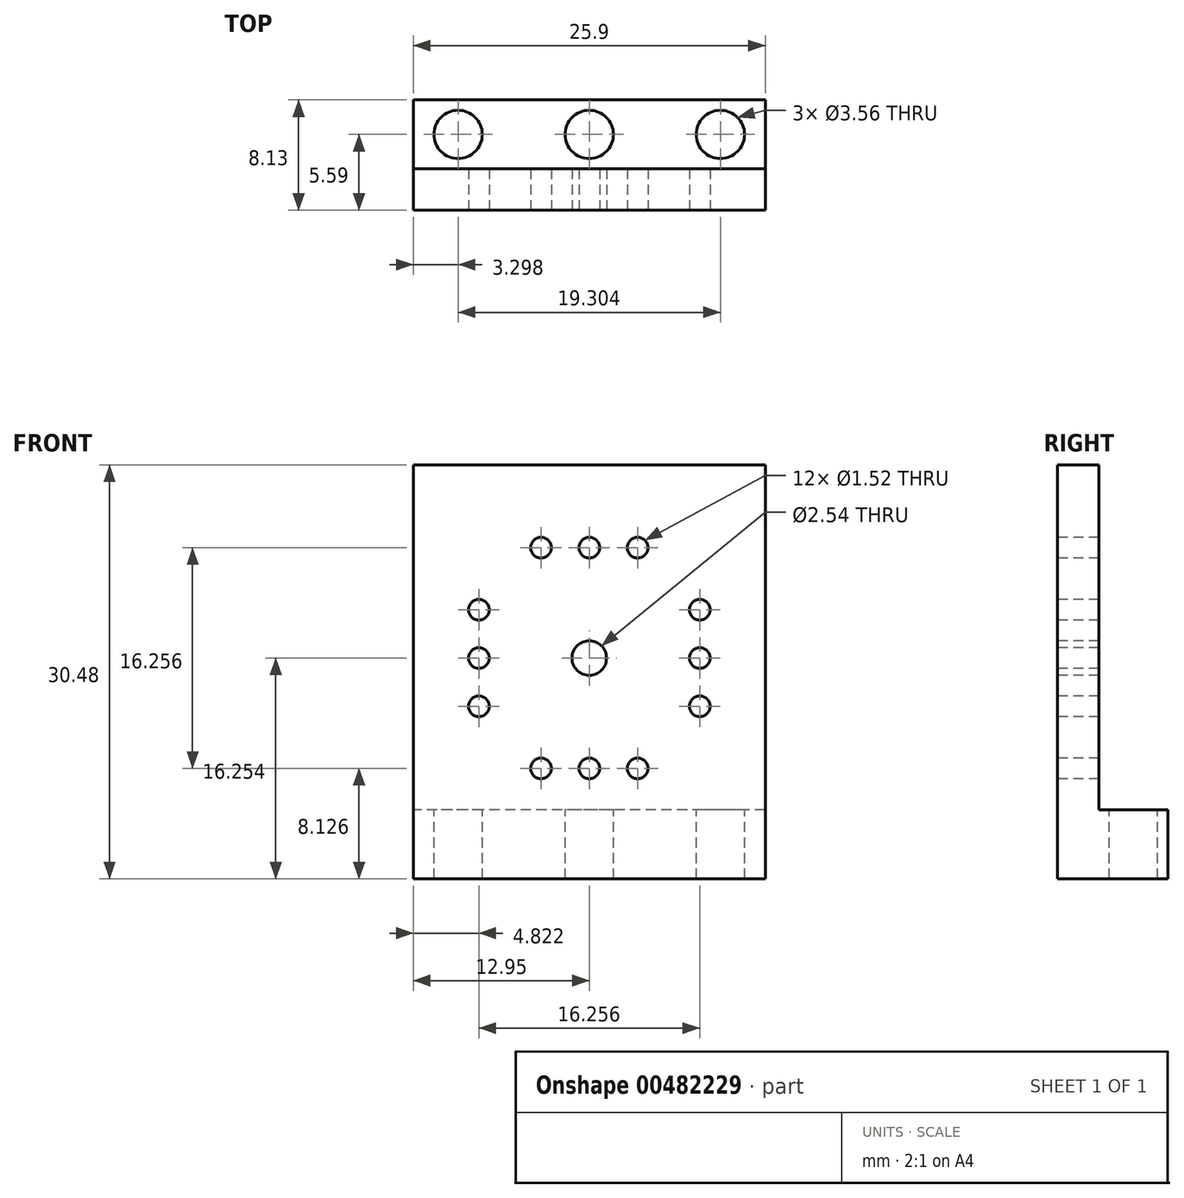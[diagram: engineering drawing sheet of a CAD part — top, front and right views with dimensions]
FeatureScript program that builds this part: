
annotation { "Feature Type Name" : "Feature", "Feature Type Description" : "" }
export const myFeature = defineFeature(function(context is Context, id is Id, definition is map)
    precondition{}
    {
        {
            var Q0;
            Q0=qCreatedBy(makeId("Top.planeOp"),FACE);
            var sketch = newSketch(context, id + "F0", { "sketchPlane" : qUnion([Q0])});
            skLineSegment(sketch, "E0.bottom", {"start": v(12.95, -2.54) * mm, "end": v(-12.95, -2.54) * mm});
            skLineSegment(sketch, "E0.top", {"start": v(12.95, 2.54) * mm, "end": v(-12.95, 2.54) * mm});
            skLineSegment(sketch, "E0.left", {"start": v(12.95, -2.54) * mm, "end": v(12.95, 2.54) * mm});
            skLineSegment(sketch, "E0.right", {"start": v(-12.95, -2.54) * mm, "end": v(-12.95, 2.54) * mm});
            skPoint(sketch, "E0.middle", {"position": v(0, 0) * mm});
            skSolve(sketch);
        }
        {
            var Q0;
            Q0=makeQuery(id+"F0.imprint","IMPRINT",FACE,{"disambiguationData":[TD([[makeQuery(id+"F0.imprint","IMPRINT",EDGE,{"derivedFrom":sQuery(id+"F0.wireOp",EDGE,"E0.bottom")}),-1.0]])]});
            extrude(context, id + "F1", {"entities" : qUnion([Q0]), "depth" : 3.05 * mm, "offsetDistance" : 25.4 * mm});
        }
        {
            var Q0;
            Q0=makeQuery(id+"F1.opExtrude","CAP_FACE",FACE,{"disambiguationData":[OSD([sQuery(id+"F0.wireOp",EDGE,"E0.bottom"),sQuery(id+"F0.wireOp",EDGE,"E0.top"),sQuery(id+"F0.wireOp",EDGE,"E0.left"),sQuery(id+"F0.wireOp",EDGE,"E0.right"),sQuery(id+"F0.wireOp",EDGE,"ECqnyMhG-ZqCw-lVKU-5K82-t7OwZ42GTA7S"),sQuery(id+"F0.wireOp",EDGE,"ETbxdbPF-hSaj-Dxkm-HRdA-5ysr9ZSDNqnm"),sQuery(id+"F0.wireOp",EDGE,"34JrhMYP-6Hn9-NnZh-YPzR-vf7p9WkIFMlo"),sQuery(id+"F0.wireOp",EDGE,"8XUWhUaj-u6eA-AcAP-s870-GFgfplMEWbZO"),sQuery(id+"F0.wireOp",EDGE,"gE9tco70-9m3o-ymKY-Motd-4k7T0K6csBKl"),sQuery(id+"F0.wireOp",EDGE,"LZpOMBkO-CBRY-Xdtn-sFue-zcv9gvVc74Jv"),sQuery(id+"F0.wireOp",EDGE,"wF5bNxiP-etsM-gzZz-KFGm-VdeNGUrKTyjR"),sQuery(id+"F0.wireOp",EDGE,"slwZwe0m-JLsY-K3UO-sD0j-G2nx1glqn7xV"),sQuery(id+"F0.wireOp",EDGE,"vA38pzm4-lHu6-xw8D-woKk-lmHSMaFGLTDd")])],"isStart":true});
            var sketch = newSketch(context, id + "F2", { "sketchPlane" : qUnion([Q0])});
            skLineSegment(sketch, "E1.bottom", {"start": v(-12.95, 2.54) * mm, "end": v(12.95, 2.54) * mm});
            skLineSegment(sketch, "E1.top", {"start": v(-12.95, 5.59) * mm, "end": v(12.95, 5.59) * mm});
            skLineSegment(sketch, "E1.left", {"start": v(-12.95, 2.54) * mm, "end": v(-12.95, 5.59) * mm});
            skLineSegment(sketch, "E1.right", {"start": v(12.95, 2.54) * mm, "end": v(12.95, 5.59) * mm});
            skSolve(sketch);
        }
        {
            var Q0;
            Q0=makeQuery(id+"F2.imprint","IMPRINT",FACE,{"disambiguationData":[TD([[makeQuery(id+"F2.imprint","IMPRINT",EDGE,{"derivedFrom":sQuery(id+"F2.wireOp",EDGE,"E1.bottom")}),-1.0]])]});
            extrude(context, id + "F3", {"entities" : qUnion([Q0]), "operationType" : NewBodyOperationType.ADD, "oppositeDirection" : true, "depth" : 28.45 * mm, "offsetDistance" : 25.4 * mm});
        }
        {
            var Q0;
            Q0=makeQuery(id+"F3.opExtrude","SWEPT_FACE",FACE,{"disambiguationData":[OSD([sQuery(id+"F2.wireOp",EDGE,"E1.top")])]});
            var sketch = newSketch(context, id + "F4", { "sketchPlane" : qUnion([Q0])});
            skLineSegment(sketch, "E2.bottom", {"start": v(12.95, 0) * mm, "end": v(-12.95, 0) * mm});
            skLineSegment(sketch, "E2.top", {"start": v(12.95, 28.45) * mm, "end": v(-12.95, 28.45) * mm});
            skLineSegment(sketch, "E2.left", {"start": v(12.95, 0) * mm, "end": v(12.95, 28.45) * mm});
            skLineSegment(sketch, "E2.right", {"start": v(-12.95, 0) * mm, "end": v(-12.95, 28.45) * mm});
            skPoint(sketch, "E2.middle", {"position": v(0, 14.22) * mm});
            skCircle(sketch, "E3", {"center": v(0, 14.22) * mm, "radius": 9.97 * mm});
            skCircle(sketch, "E4", {"center": v(0, 14.22) * mm, "radius": 1.27 * mm});
            skCircle(sketch, "E5", {"center": v(0, 22.35) * mm, "radius": 0.76 * mm});
            skCircle(sketch, "E6", {"center": v(0, 6.1) * mm, "radius": 0.76 * mm});
            skCircle(sketch, "E7", {"center": v(8.13, 14.22) * mm, "radius": 0.76 * mm});
            skCircle(sketch, "E8", {"center": v(-8.13, 14.22) * mm, "radius": 0.76 * mm});
            skCircle(sketch, "E9", {"center": v(-8.13, 10.67) * mm, "radius": 0.76 * mm});
            skCircle(sketch, "E10", {"center": v(-8.13, 17.78) * mm, "radius": 0.76 * mm});
            skCircle(sketch, "E11", {"center": v(3.56, 22.35) * mm, "radius": 0.76 * mm});
            skCircle(sketch, "E12", {"center": v(-3.56, 22.35) * mm, "radius": 0.76 * mm});
            skCircle(sketch, "E13", {"center": v(8.13, 17.78) * mm, "radius": 0.76 * mm});
            skCircle(sketch, "E14", {"center": v(8.13, 10.67) * mm, "radius": 0.76 * mm});
            skCircle(sketch, "E15", {"center": v(3.56, 6.1) * mm, "radius": 0.76 * mm});
            skCircle(sketch, "E16", {"center": v(-3.56, 6.1) * mm, "radius": 0.76 * mm});
            skSolve(sketch);
        }
        {
            var Q0;
            Q0=makeQuery(id+"F4.imprint","IMPRINT",FACE,{"disambiguationData":[TD([[makeQuery(id+"F4.imprint","IMPRINT",EDGE,{"derivedFrom":sQuery(id+"F4.wireOp",EDGE,"E8")}),1.0]])]});
            var Q1;
            Q1=makeQuery(id+"F4.imprint","IMPRINT",FACE,{"disambiguationData":[TD([[makeQuery(id+"F4.imprint","IMPRINT",EDGE,{"derivedFrom":sQuery(id+"F4.wireOp",EDGE,"E10")}),1.0]])]});
            var Q2;
            Q2=makeQuery(id+"F4.imprint","IMPRINT",FACE,{"disambiguationData":[TD([[makeQuery(id+"F4.imprint","IMPRINT",EDGE,{"derivedFrom":sQuery(id+"F4.wireOp",EDGE,"E9")}),1.0]])]});
            var Q3;
            Q3=makeQuery(id+"F4.imprint","IMPRINT",FACE,{"disambiguationData":[TD([[makeQuery(id+"F4.imprint","IMPRINT",EDGE,{"derivedFrom":sQuery(id+"F4.wireOp",EDGE,"E16")}),1.0]])]});
            var Q4;
            Q4=makeQuery(id+"F4.imprint","IMPRINT",FACE,{"disambiguationData":[TD([[makeQuery(id+"F4.imprint","IMPRINT",EDGE,{"derivedFrom":sQuery(id+"F4.wireOp",EDGE,"E6")}),1.0]])]});
            var Q5;
            Q5=makeQuery(id+"F4.imprint","IMPRINT",FACE,{"disambiguationData":[TD([[makeQuery(id+"F4.imprint","IMPRINT",EDGE,{"derivedFrom":sQuery(id+"F4.wireOp",EDGE,"E15")}),1.0]])]});
            var Q6;
            Q6=makeQuery(id+"F4.imprint","IMPRINT",FACE,{"disambiguationData":[TD([[makeQuery(id+"F4.imprint","IMPRINT",EDGE,{"derivedFrom":sQuery(id+"F4.wireOp",EDGE,"E14")}),1.0]])]});
            var Q7;
            Q7=makeQuery(id+"F4.imprint","IMPRINT",FACE,{"disambiguationData":[TD([[makeQuery(id+"F4.imprint","IMPRINT",EDGE,{"derivedFrom":sQuery(id+"F4.wireOp",EDGE,"E7")}),1.0]])]});
            var Q8;
            Q8=makeQuery(id+"F4.imprint","IMPRINT",FACE,{"disambiguationData":[TD([[makeQuery(id+"F4.imprint","IMPRINT",EDGE,{"derivedFrom":sQuery(id+"F4.wireOp",EDGE,"E13")}),1.0]])]});
            var Q9;
            Q9=makeQuery(id+"F4.imprint","IMPRINT",FACE,{"disambiguationData":[TD([[makeQuery(id+"F4.imprint","IMPRINT",EDGE,{"derivedFrom":sQuery(id+"F4.wireOp",EDGE,"E11")}),1.0]])]});
            var Q10;
            Q10=makeQuery(id+"F4.imprint","IMPRINT",FACE,{"disambiguationData":[TD([[makeQuery(id+"F4.imprint","IMPRINT",EDGE,{"derivedFrom":sQuery(id+"F4.wireOp",EDGE,"E5")}),1.0]])]});
            var Q11;
            Q11=makeQuery(id+"F4.imprint","IMPRINT",FACE,{"disambiguationData":[TD([[makeQuery(id+"F4.imprint","IMPRINT",EDGE,{"derivedFrom":sQuery(id+"F4.wireOp",EDGE,"E12")}),1.0]])]});
            var Q12;
            Q12=makeQuery(id+"F4.imprint","IMPRINT",FACE,{"disambiguationData":[TD([[makeQuery(id+"F4.imprint","IMPRINT",EDGE,{"derivedFrom":sQuery(id+"F4.wireOp",EDGE,"E4")}),1.0]])]});
            extrude(context, id + "F5", {"entities" : qUnion([Q0, Q1, Q2, Q3, Q4, Q5, Q6, Q7, Q8, Q9, Q10, Q11, Q12]), "operationType" : NewBodyOperationType.REMOVE, "oppositeDirection" : true, "depth" : 25.4 * mm, "offsetDistance" : 25.4 * mm});
        }
        {
            var Q0;
            Q0=makeQuery(id+"F1.opExtrude","CAP_FACE",FACE,{"disambiguationData":[OSD([sQuery(id+"F0.wireOp",EDGE,"E0.bottom"),sQuery(id+"F0.wireOp",EDGE,"E0.top"),sQuery(id+"F0.wireOp",EDGE,"E0.left"),sQuery(id+"F0.wireOp",EDGE,"E0.right")])],"isStart":false});
            var sketch = newSketch(context, id + "F6", { "sketchPlane" : qUnion([Q0])});
            skCircle(sketch, "E17", {"center": v(0, 0) * mm, "radius": 1.78 * mm});
            skCircle(sketch, "E18", {"center": v(9.65, 0) * mm, "radius": 1.78 * mm});
            skCircle(sketch, "E19", {"center": v(-9.65, 0) * mm, "radius": 1.78 * mm});
            skSolve(sketch);
        }
        {
            var Q0;
            Q0=makeQuery(id+"F6.imprint","IMPRINT",FACE,{"disambiguationData":[TD([[makeQuery(id+"F6.imprint","IMPRINT",EDGE,{"derivedFrom":sQuery(id+"F6.wireOp",EDGE,"E19")}),1.0]])]});
            var Q1;
            Q1=makeQuery(id+"F6.imprint","IMPRINT",FACE,{"disambiguationData":[TD([[makeQuery(id+"F6.imprint","IMPRINT",EDGE,{"derivedFrom":sQuery(id+"F6.wireOp",EDGE,"E17")}),1.0]])]});
            var Q2;
            Q2=makeQuery(id+"F6.imprint","IMPRINT",FACE,{"disambiguationData":[TD([[makeQuery(id+"F6.imprint","IMPRINT",EDGE,{"derivedFrom":sQuery(id+"F6.wireOp",EDGE,"E18")}),1.0]])]});
            extrude(context, id + "F7", {"entities" : qUnion([Q0, Q1, Q2]), "operationType" : NewBodyOperationType.REMOVE, "oppositeDirection" : true, "depth" : 25.4 * mm, "offsetDistance" : 25.4 * mm});
        }
        {
            var Q0;
            Q0=makeQuery(id+"F3.boolean.opBoolean","MERGE",FACE,{"derivedFrom":[makeQuery(id+"F1.opExtrude","CAP_FACE",FACE,{"disambiguationData":[OSD([sQuery(id+"F0.wireOp",EDGE,"E0.bottom"),sQuery(id+"F0.wireOp",EDGE,"E0.top"),sQuery(id+"F0.wireOp",EDGE,"E0.left"),sQuery(id+"F0.wireOp",EDGE,"E0.right")])],"isStart":true}),makeQuery(id+"F3.opExtrude","CAP_FACE",FACE,{"disambiguationData":[OSD([sQuery(id+"F2.wireOp",EDGE,"E1.bottom"),sQuery(id+"F2.wireOp",EDGE,"E1.top"),sQuery(id+"F2.wireOp",EDGE,"E1.left"),sQuery(id+"F2.wireOp",EDGE,"E1.right")])],"isStart":true})]});
            extrude(context, id + "F8", {"entities" : qUnion([Q0]), "operationType" : NewBodyOperationType.ADD, "depth" : 2.03 * mm, "offsetDistance" : 25.4 * mm});
        }
    });
